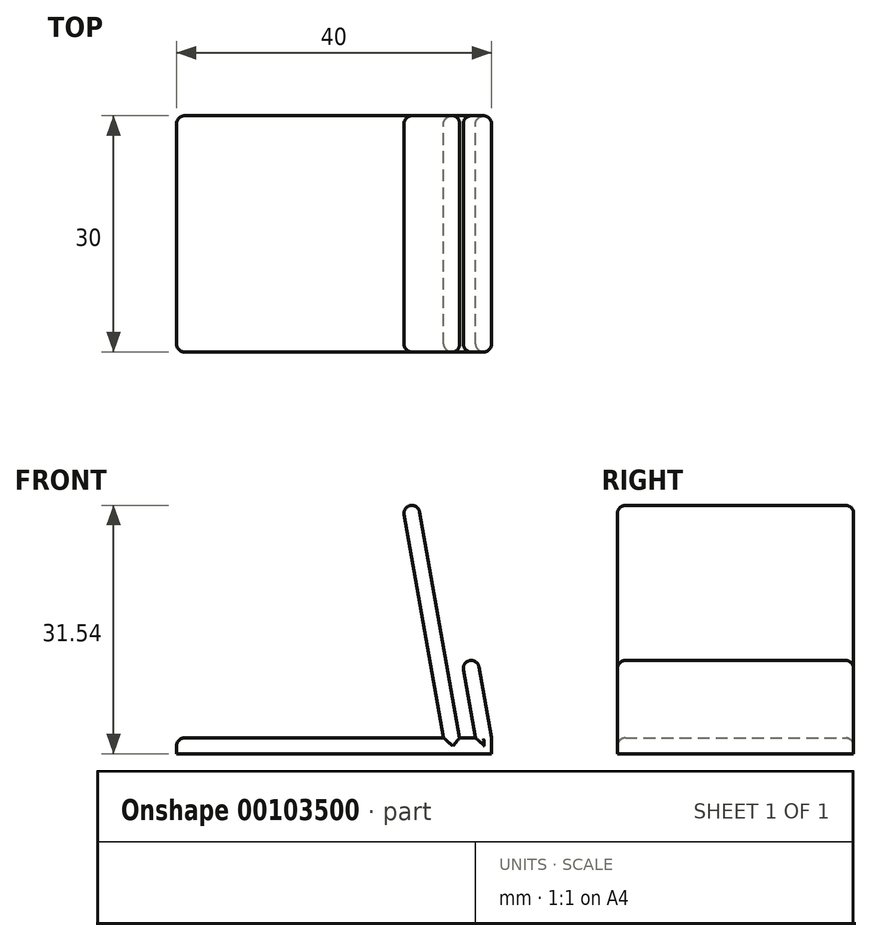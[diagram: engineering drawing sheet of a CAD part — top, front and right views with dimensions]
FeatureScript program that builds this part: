
annotation { "Feature Type Name" : "Feature", "Feature Type Description" : "" }
export const myFeature = defineFeature(function(context is Context, id is Id, definition is map)
    precondition{}
    {
        {
            var Q0;
            Q0=qCreatedBy(makeId("Front.planeOp"),FACE);
            var sketch = newSketch(context, id + "F0", { "sketchPlane" : qUnion([Q0])});
            skLineSegment(sketch, "E0.bottom", {"start": v(-20, 0) * mm, "end": v(20, 0) * mm});
            skLineSegment(sketch, "E0.top", {"start": v(-20, 2) * mm, "end": v(13.9, 2) * mm});
            skLineSegment(sketch, "E0.left", {"start": v(-20, 0) * mm, "end": v(-20, 2) * mm});
            skLineSegment(sketch, "E0.right", {"start": v(20, 0) * mm, "end": v(20, 2) * mm});
            skLineSegment(sketch, "E1", {"start": v(20, 2) * mm, "end": v(18.26, 11.85) * mm});
            skLineSegment(sketch, "E2", {"start": v(18.26, 11.85) * mm, "end": v(16.23, 11.85) * mm});
            skLineSegment(sketch, "E3", {"start": v(16.23, 11.85) * mm, "end": v(17.97, 2) * mm});
            skLineSegment(sketch, "E4", {"start": v(15.94, 2) * mm, "end": v(10.73, 31.54) * mm});
            skLineSegment(sketch, "E5", {"start": v(10.73, 31.54) * mm, "end": v(8.7, 31.54) * mm});
            skLineSegment(sketch, "E6", {"start": v(8.7, 31.54) * mm, "end": v(13.9, 2) * mm});
            skLineSegment(sketch, "E7.trimOffspring", {"start": v(15.94, 2) * mm, "end": v(17.97, 2) * mm});
            skSolve(sketch);
        }
        {
            var Q0;
            Q0=makeQuery(id+"F0.imprint","IMPRINT",FACE,{"disambiguationData":[TD([[makeQuery(id+"F0.imprint","IMPRINT",EDGE,{"derivedFrom":sQuery(id+"F0.wireOp",EDGE,"E0.bottom")}),1.0]])]});
            extrude(context, id + "F1", {"entities" : qUnion([Q0]), "endBound" : BoundingType.SYMMETRIC, "depth" : 30 * mm});
        }
        {
            var Q0;
            Q0=makeQuery(id+"F1.opExtrude","CAP_EDGE",EDGE,{"disambiguationData":[OSD([sQuery(id+"F0.wireOp",EDGE,"E0.top")])],"isStart":false});
            var Q1;
            Q1=makeQuery(id+"F1.opExtrude","SWEPT_EDGE",EDGE,{"disambiguationData":[OSD([sQuery(id+"F0.wireOp",EDGE,"E0.top"),sQuery(id+"F0.wireOp",EDGE,"E0.left")])]});
            var Q2;
            Q2=makeQuery(id+"F1.opExtrude","CAP_EDGE",EDGE,{"disambiguationData":[OSD([sQuery(id+"F0.wireOp",EDGE,"E0.top")])],"isStart":true});
            var Q3;
            Q3=makeQuery(id+"F1.opExtrude","CAP_EDGE",EDGE,{"disambiguationData":[OSD([sQuery(id+"F0.wireOp",EDGE,"E6")])],"isStart":false});
            var Q4;
            Q4=makeQuery(id+"F1.opExtrude","CAP_EDGE",EDGE,{"disambiguationData":[OSD([sQuery(id+"F0.wireOp",EDGE,"E6")])],"isStart":true});
            var Q5;
            Q5=makeQuery(id+"F1.opExtrude","SWEPT_EDGE",EDGE,{"disambiguationData":[OSD([sQuery(id+"F0.wireOp",EDGE,"E5"),sQuery(id+"F0.wireOp",EDGE,"E6")])]});
            var Q6;
            Q6=makeQuery(id+"F1.opExtrude","CAP_EDGE",EDGE,{"disambiguationData":[OSD([sQuery(id+"F0.wireOp",EDGE,"E0.left")])],"isStart":true});
            var Q7;
            Q7=makeQuery(id+"F1.opExtrude","CAP_EDGE",EDGE,{"disambiguationData":[OSD([sQuery(id+"F0.wireOp",EDGE,"E0.left")])],"isStart":false});
            var Q8;
            Q8=makeQuery(id+"F1.opExtrude","CAP_EDGE",EDGE,{"disambiguationData":[OSD([sQuery(id+"F0.wireOp",EDGE,"E4")])],"isStart":false});
            var Q9;
            Q9=makeQuery(id+"F1.opExtrude","SWEPT_EDGE",EDGE,{"disambiguationData":[OSD([sQuery(id+"F0.wireOp",EDGE,"E4"),sQuery(id+"F0.wireOp",EDGE,"E5")])]});
            var Q10;
            Q10=makeQuery(id+"F1.opExtrude","CAP_EDGE",EDGE,{"disambiguationData":[OSD([sQuery(id+"F0.wireOp",EDGE,"E4")])],"isStart":true});
            var Q11;
            Q11=makeQuery(id+"F1.opExtrude","CAP_EDGE",EDGE,{"disambiguationData":[OSD([sQuery(id+"F0.wireOp",EDGE,"E7.trimOffspring")])],"isStart":true});
            var Q12;
            Q12=makeQuery(id+"F1.opExtrude","CAP_EDGE",EDGE,{"disambiguationData":[OSD([sQuery(id+"F0.wireOp",EDGE,"E3")])],"isStart":true});
            var Q13;
            Q13=makeQuery(id+"F1.opExtrude","CAP_EDGE",EDGE,{"disambiguationData":[OSD([sQuery(id+"F0.wireOp",EDGE,"E2")])],"isStart":true});
            var Q14;
            Q14=makeQuery(id+"F1.opExtrude","CAP_EDGE",EDGE,{"disambiguationData":[OSD([sQuery(id+"F0.wireOp",EDGE,"E1")])],"isStart":true});
            var Q15;
            Q15=makeQuery(id+"F1.opExtrude","CAP_EDGE",EDGE,{"disambiguationData":[OSD([sQuery(id+"F0.wireOp",EDGE,"E0.right")])],"isStart":true});
            var Q16;
            Q16=makeQuery(id+"F1.opExtrude","CAP_EDGE",EDGE,{"disambiguationData":[OSD([sQuery(id+"F0.wireOp",EDGE,"E7.trimOffspring")])],"isStart":false});
            var Q17;
            Q17=makeQuery(id+"F1.opExtrude","CAP_EDGE",EDGE,{"disambiguationData":[OSD([sQuery(id+"F0.wireOp",EDGE,"E3")])],"isStart":false});
            var Q18;
            Q18=makeQuery(id+"F1.opExtrude","CAP_EDGE",EDGE,{"disambiguationData":[OSD([sQuery(id+"F0.wireOp",EDGE,"E2")])],"isStart":false});
            var Q19;
            Q19=makeQuery(id+"F1.opExtrude","CAP_EDGE",EDGE,{"disambiguationData":[OSD([sQuery(id+"F0.wireOp",EDGE,"E1")])],"isStart":false});
            var Q20;
            Q20=makeQuery(id+"F1.opExtrude","CAP_EDGE",EDGE,{"disambiguationData":[OSD([sQuery(id+"F0.wireOp",EDGE,"E0.right")])],"isStart":false});
            var Q21;
            Q21=makeQuery(id+"F1.opExtrude","SWEPT_EDGE",EDGE,{"disambiguationData":[OSD([sQuery(id+"F0.wireOp",EDGE,"E1"),sQuery(id+"F0.wireOp",EDGE,"E2")])]});
            var Q22;
            Q22=makeQuery(id+"F1.opExtrude","SWEPT_EDGE",EDGE,{"disambiguationData":[OSD([sQuery(id+"F0.wireOp",EDGE,"E2"),sQuery(id+"F0.wireOp",EDGE,"E3")])]});
            var Q23;
            Q23=makeQuery(id+"F1.opExtrude","SWEPT_EDGE",EDGE,{"disambiguationData":[OSD([sQuery(id+"F0.wireOp",EDGE,"E0.right"),sQuery(id+"F0.wireOp",EDGE,"E1")])]});
            var Q24;
            Q24=makeQuery(id+"F1.opExtrude","CAP_EDGE",EDGE,{"disambiguationData":[OSD([sQuery(id+"F0.wireOp",EDGE,"E5")])],"isStart":true});
            var Q25;
            Q25=makeQuery(id+"F1.opExtrude","CAP_EDGE",EDGE,{"disambiguationData":[OSD([sQuery(id+"F0.wireOp",EDGE,"E5")])],"isStart":false});
            fillet(context, id + "F2", {"entities" : qUnion([Q0, Q1, Q2, Q3, Q4, Q5, Q6, Q7, Q8, Q9, Q10, Q11, Q12, Q13, Q14, Q15, Q16, Q17, Q18, Q19, Q20, Q21, Q22, Q23, Q24, Q25]), "radius" : 1 * mm, "tangentPropagation" : true, "allowEdgeOverflow" : false});
        }
    });
